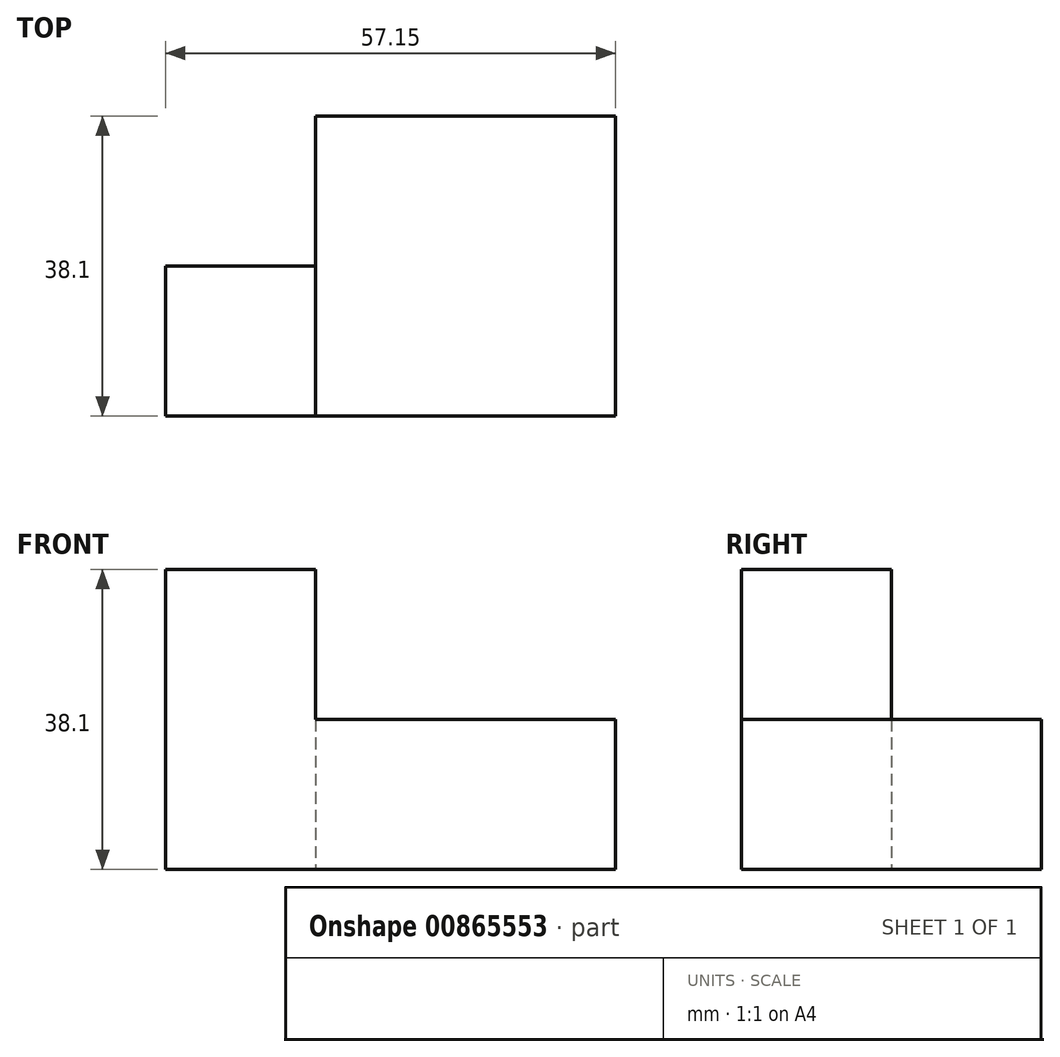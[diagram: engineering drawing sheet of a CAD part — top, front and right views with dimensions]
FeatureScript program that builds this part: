
annotation { "Feature Type Name" : "Feature", "Feature Type Description" : "" }
export const myFeature = defineFeature(function(context is Context, id is Id, definition is map)
    precondition{}
    {
        {
            var Q0;
            Q0=qCreatedBy(makeId("Front.planeOp"),FACE);
            var sketch = newSketch(context, id + "F0", { "sketchPlane" : qUnion([Q0])});
            skLineSegment(sketch, "E0", {"start": v(-25.4, -19.05) * mm, "end": v(31.75, -19.05) * mm});
            skLineSegment(sketch, "E1", {"start": v(31.75, -19.05) * mm, "end": v(31.75, 0) * mm});
            skLineSegment(sketch, "E2", {"start": v(31.75, 0) * mm, "end": v(-6.35, 0) * mm});
            skLineSegment(sketch, "E3", {"start": v(-6.35, 0) * mm, "end": v(-6.35, 19.05) * mm});
            skLineSegment(sketch, "E4", {"start": v(-6.35, 19.05) * mm, "end": v(-25.4, 19.05) * mm});
            skLineSegment(sketch, "E5", {"start": v(-25.4, 19.05) * mm, "end": v(-25.4, -19.05) * mm});
            skSolve(sketch);
        }
        {
            var Q0;
            Q0=makeQuery(id+"F0.imprint","IMPRINT",FACE,{"disambiguationData":[TD([[makeQuery(id+"F0.imprint","IMPRINT",EDGE,{"derivedFrom":sQuery(id+"F0.wireOp",EDGE,"E0")}),1.0]])]});
            extrude(context, id + "F1", {"entities" : qUnion([Q0]), "depth" : 19.05 * mm, "offsetDistance" : 25.4 * mm});
        }
        {
            var Q0;
            Q0=makeQuery(id+"F1.opExtrude","CAP_FACE",FACE,{"disambiguationData":[OSD([sQuery(id+"F0.wireOp",EDGE,"E0"),sQuery(id+"F0.wireOp",EDGE,"E1"),sQuery(id+"F0.wireOp",EDGE,"E2"),sQuery(id+"F0.wireOp",EDGE,"E3"),sQuery(id+"F0.wireOp",EDGE,"E4"),sQuery(id+"F0.wireOp",EDGE,"E5")])],"isStart":true});
            var sketch = newSketch(context, id + "F2", { "sketchPlane" : qUnion([Q0])});
            skLineSegment(sketch, "E6", {"start": v(6.35, 0) * mm, "end": v(6.35, -19.05) * mm});
            skSolve(sketch);
        }
        {
            var Q0;
            {var subQ0=sQuery(id+"F2.wireOp",EDGE,"E6");Q0=makeQuery(id+"F2.imprint","IMPRINT",FACE,{"disambiguationData":[TD([[makeQuery(id+"F2.imprint","IMPRINT",EDGE,{"derivedFrom":subQ0}),-1.0]])]});}
            extrude(context, id + "F3", {"entities" : qUnion([Q0]), "operationType" : NewBodyOperationType.ADD, "depth" : 19.05 * mm, "offsetDistance" : 25.4 * mm});
        }
    });
